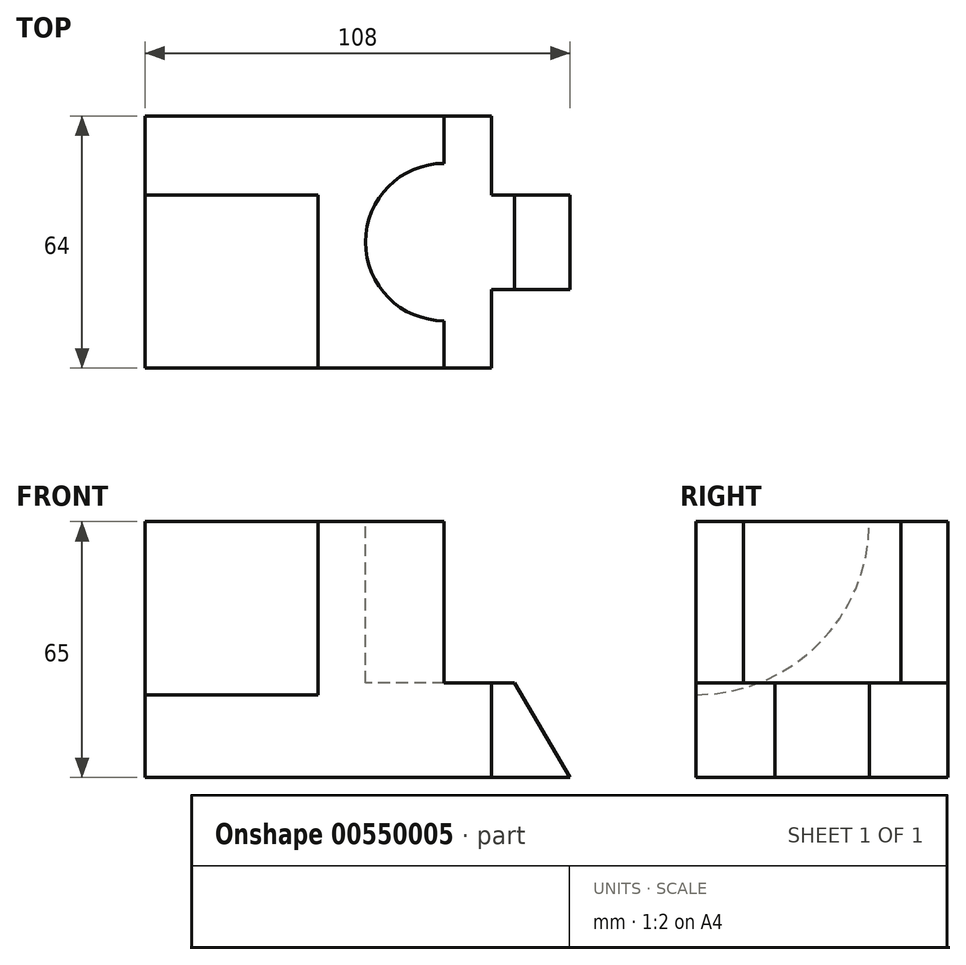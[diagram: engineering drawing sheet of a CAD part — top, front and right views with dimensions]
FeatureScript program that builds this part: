
annotation { "Feature Type Name" : "Feature", "Feature Type Description" : "" }
export const myFeature = defineFeature(function(context is Context, id is Id, definition is map)
    precondition{}
    {
        {
            var Q0;
            Q0=qCreatedBy(makeId("Top.planeOp"),FACE);
            var sketch = newSketch(context, id + "F0", { "sketchPlane" : qUnion([Q0])});
            skLineSegment(sketch, "E0.bottom", {"start": v(44, 32) * mm, "end": v(-44, 32) * mm});
            skLineSegment(sketch, "E0.top", {"start": v(44, -32) * mm, "end": v(-44, -32) * mm});
            skLineSegment(sketch, "E0.left", {"start": v(44, 32) * mm, "end": v(44, -32) * mm});
            skLineSegment(sketch, "E0.right", {"start": v(-44, 32) * mm, "end": v(-44, -32) * mm});
            skPoint(sketch, "E0.middle", {"position": v(0, 0) * mm});
            skLineSegment(sketch, "E1", {"start": v(44, -32) * mm, "end": v(32, -32) * mm});
            skLineSegment(sketch, "E2", {"start": v(32, -32) * mm, "end": v(32, 32) * mm});
            skLineSegment(sketch, "E3", {"start": v(32, -32) * mm, "end": v(0, -32) * mm});
            skLineSegment(sketch, "E4", {"start": v(-44, 32) * mm, "end": v(-44, 12) * mm});
            skLineSegment(sketch, "E5", {"start": v(-44, 12) * mm, "end": v(0, 12) * mm});
            skLineSegment(sketch, "E6", {"start": v(0, 12) * mm, "end": v(0, -32) * mm});
            skSolve(sketch);
        }
        {
            var Q0;
            {var subQ0=sQuery(id+"F0.wireOp",EDGE,"E0.left");Q0=makeQuery(id+"F0.imprint","IMPRINT",FACE,{"disambiguationData":[TD([[makeQuery(id+"F0.imprint","IMPRINT",EDGE,{"derivedFrom":subQ0}),-1.0]])]});}
            extrude(context, id + "F1", {"entities" : qUnion([Q0]), "depth" : 24 * mm, "offsetDistance" : 25 * mm});
        }
        {
            var Q0;
            {var subQ1=sQuery(id+"F0.wireOp",EDGE,"E2");Q0=makeQuery(id+"F0.imprint","IMPRINT",FACE,{"disambiguationData":[TD([[makeQuery(id+"F0.imprint","IMPRINT",EDGE,{"derivedFrom":subQ1}),1.0]])]});}
            extrude(context, id + "F2", {"entities" : qUnion([Q0]), "operationType" : NewBodyOperationType.ADD, "depth" : 65 * mm, "offsetDistance" : 25 * mm});
        }
        {
            var Q0;
            Q0=makeQuery(id+"F1.opExtrude","SWEPT_FACE",FACE,{"disambiguationData":[OSD([sQuery(id+"F0.wireOp",EDGE,"E0.left")])]});
            var sketch = newSketch(context, id + "F3", { "sketchPlane" : qUnion([Q0])});
            skLineSegment(sketch, "E7", {"start": v(-32, 0) * mm, "end": v(-12, 0) * mm});
            skLineSegment(sketch, "E8", {"start": v(-12, 0) * mm, "end": v(-12, 24) * mm});
            skLineSegment(sketch, "E9", {"start": v(-12, 24) * mm, "end": v(12, 24) * mm});
            skLineSegment(sketch, "E10", {"start": v(12, 24) * mm, "end": v(12, 0) * mm});
            skLineSegment(sketch, "E11", {"start": v(12, 0) * mm, "end": v(-13.04, 0) * mm});
            skSolve(sketch);
        }
        {
            var Q0;
            Q0 = qSketchRegion(id + "F3", true);
            extrude(context, id + "F4", {"entities" : qUnion([Q0]), "operationType" : NewBodyOperationType.ADD, "depth" : 20 * mm, "offsetDistance" : 25 * mm});
        }
        {
            var Q0;
            Q0=makeQuery(id+"F4.opExtrude","SWEPT_FACE",FACE,{"disambiguationData":[OSD([sQuery(id+"F3.wireOp",EDGE,"E8")])]});
            var sketch = newSketch(context, id + "F5", { "sketchPlane" : qUnion([Q0])});
            skLineSegment(sketch, "E12", {"start": v(49.8, 24) * mm, "end": v(64, 0) * mm});
            skSolve(sketch);
        }
        {
            var Q0;
            {var subQ0=sQuery(id+"F5.wireOp",EDGE,"E12");Q0=makeQuery(id+"F5.imprint","IMPRINT",FACE,{"disambiguationData":[TD([[makeQuery(id+"F5.imprint","IMPRINT",EDGE,{"derivedFrom":subQ0}),1.0]])]});}
            extrude(context, id + "F6", {"entities" : qUnion([Q0]), "operationType" : NewBodyOperationType.REMOVE, "oppositeDirection" : true, "depth" : 37.6 * mm, "offsetDistance" : 25 * mm});
        }
        {
            var Q0;
            Q0=makeQuery(id+"F2.opExtrude","CAP_FACE",FACE,{"disambiguationData":[OSD([sQuery(id+"F0.wireOp",EDGE,"E0.bottom"),sQuery(id+"F0.wireOp",EDGE,"E2"),sQuery(id+"F0.wireOp",EDGE,"E3"),sQuery(id+"F0.wireOp",EDGE,"E4"),sQuery(id+"F0.wireOp",EDGE,"E5"),sQuery(id+"F0.wireOp",EDGE,"E6")])],"isStart":false});
            var sketch = newSketch(context, id + "F7", { "sketchPlane" : qUnion([Q0])});
            skLineSegment(sketch, "E13", {"start": v(32, -32) * mm, "end": v(32, -20) * mm});
            skLineSegment(sketch, "E14", {"start": v(32, 32) * mm, "end": v(32, 20) * mm});
            skLineSegment(sketch, "E15", {"start": v(32, 20) * mm, "end": v(32, -20) * mm});
            skCircle(sketch, "E16", {"center": v(32, 0) * mm, "radius": 20 * mm});
            skSolve(sketch);
        }
        {
            var Q0;
            {var subQ0=sQuery(id+"F7.wireOp",EDGE,"E15");Q0=makeQuery(id+"F7.imprint","IMPRINT",FACE,{"disambiguationData":[TD([[makeQuery(id+"F7.imprint","IMPRINT",EDGE,{"derivedFrom":subQ0}),1.0]])]});}
            extrude(context, id + "F8", {"entities" : qUnion([Q0]), "operationType" : NewBodyOperationType.REMOVE, "oppositeDirection" : true, "depth" : 41 * mm, "offsetDistance" : 25 * mm});
        }
        {
            var Q0;
            Q0=makeQuery(id+"F0.imprint","IMPRINT",FACE,{"disambiguationData":[TD([[makeQuery(id+"F0.imprint","IMPRINT",EDGE,{"derivedFrom":sQuery(id+"F0.wireOp",EDGE,"E0.top")}),-1.0]])]});
            var sketch = newSketch(context, id + "F9", { "sketchPlane" : qUnion([Q0])});
            skLineSegment(sketch, "E17.0.0", {"start": v(0, 12) * mm, "end": v(-44, 12) * mm});
            skLineSegment(sketch, "E17.0.1", {"start": v(-44, 12) * mm, "end": v(-44, -32) * mm});
            skLineSegment(sketch, "E17.0.2", {"start": v(-44, -32) * mm, "end": v(0, -32) * mm});
            skLineSegment(sketch, "E17.0.3", {"start": v(0, -32) * mm, "end": v(0, 12) * mm});
            skSolve(sketch);
        }
        {
            var Q0;
            Q0 = qSketchRegion(id + "F9", true);
            extrude(context, id + "F10", {"entities" : qUnion([Q0]), "operationType" : NewBodyOperationType.ADD, "depth" : 12 * mm, "offsetDistance" : 25 * mm});
        }
        {
            var Q0;
            Q0=makeQuery(id+"F10.opExtrude","CAP_FACE",FACE,{"disambiguationData":[OSD([sQuery(id+"F9.wireOp",EDGE,"E17.0.0"),sQuery(id+"F9.wireOp",EDGE,"E17.0.1"),sQuery(id+"F9.wireOp",EDGE,"E17.0.2"),sQuery(id+"F9.wireOp",EDGE,"E17.0.3")])],"isStart":false});
            var sketch = newSketch(context, id + "F11", { "sketchPlane" : qUnion([Q0])});
            skLineSegment(sketch, "E18.bottom", {"start": v(-44, -32) * mm, "end": v(0, -32) * mm});
            skLineSegment(sketch, "E18.top", {"start": v(-44, 12) * mm, "end": v(0, 12) * mm});
            skLineSegment(sketch, "E18.left", {"start": v(-44, -32) * mm, "end": v(-44, 12) * mm});
            skLineSegment(sketch, "E18.right", {"start": v(0, -32) * mm, "end": v(0, 12) * mm});
            skSolve(sketch);
        }
        {
            var Q0;
            Q0 = qSketchRegion(id + "F11", true);
            extrude(context, id + "F12", {"entities" : qUnion([Q0]), "operationType" : NewBodyOperationType.ADD, "depth" : 53 * mm, "offsetDistance" : 25 * mm});
        }
        {
            var Q0;
            Q0=makeQuery(id+"F12.boolean.opBoolean","MERGE",FACE,{"derivedFrom":[makeQuery(id+"F10.boolean.opBoolean","MERGE",FACE,{"derivedFrom":[makeQuery(id+"F2.opExtrude","SWEPT_FACE",FACE,{"disambiguationData":[OSD([sQuery(id+"F0.wireOp",EDGE,"E4")])]}),makeQuery(id+"F10.opExtrude","SWEPT_FACE",FACE,{"disambiguationData":[OSD([sQuery(id+"F9.wireOp",EDGE,"E17.0.1")])]})]}),makeQuery(id+"F12.opExtrude","SWEPT_FACE",FACE,{"disambiguationData":[OSD([sQuery(id+"F11.wireOp",EDGE,"E18.left")])]})]});
            var sketch = newSketch(context, id + "F13", { "sketchPlane" : qUnion([Q0])});
            skPoint(sketch, "E19", {"position": v(-12, 65) * mm});
            skLineSegment(sketch, "E20", {"start": v(-12, 65) * mm, "end": v(-12, 21) * mm});
            skLineSegment(sketch, "E21", {"start": v(-12, 21) * mm, "end": v(32, 21) * mm});
            skArc(sketch, "E22", {"start": v(-12, 65) * mm, "mid": v(0.89, 33.89) * mm, "end": v(32, 21) * mm});
            skSolve(sketch);
        }
        {
            var Q0;
            {var subQ0=sQuery(id+"F13.wireOp",EDGE,"E22");Q0=makeQuery(id+"F13.imprint","IMPRINT",FACE,{"disambiguationData":[TD([[makeQuery(id+"F13.imprint","IMPRINT",EDGE,{"derivedFrom":subQ0}),1.0]])]});}
            extrude(context, id + "F14", {"entities" : qUnion([Q0]), "operationType" : NewBodyOperationType.REMOVE, "oppositeDirection" : true, "depth" : 44 * mm, "offsetDistance" : 25 * mm});
        }
    });
